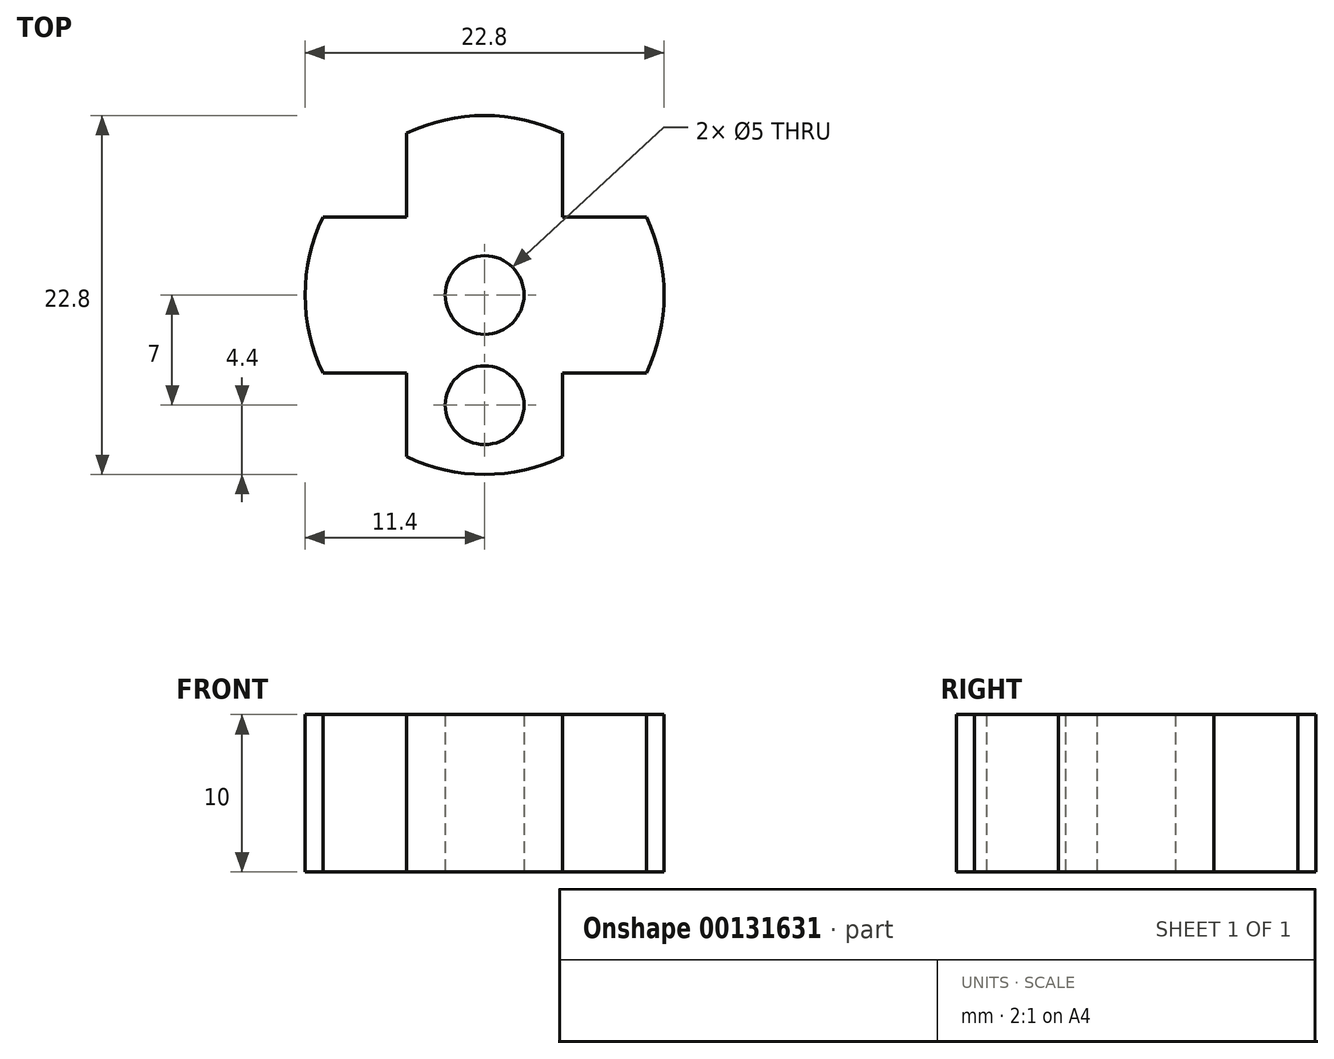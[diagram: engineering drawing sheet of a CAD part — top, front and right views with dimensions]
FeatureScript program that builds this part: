
annotation { "Feature Type Name" : "Feature", "Feature Type Description" : "" }
export const myFeature = defineFeature(function(context is Context, id is Id, definition is map)
    precondition{}
    {
        {
            var Q0;
            Q0=qCreatedBy(makeId("Top.planeOp"),FACE);
            var sketch = newSketch(context, id + "F0", { "sketchPlane" : qUnion([Q0])});
            skCircle(sketch, "E0", {"center": v(0, 0) * mm, "radius": 11.4 * mm});
            skCircle(sketch, "E1", {"center": v(0, 0) * mm, "radius": 2.5 * mm});
            skCircle(sketch, "E2", {"center": v(0, 0) * mm, "radius": 7 * mm, "construction": true});
            skCircle(sketch, "E3", {"center": v(0, -7) * mm, "radius": 2.5 * mm});
            skLineSegment(sketch, "E4", {"start": v(-4.95, -10.27) * mm, "end": v(-4.95, -4.95) * mm});
            skLineSegment(sketch, "E5", {"start": v(-4.95, -4.95) * mm, "end": v(-10.27, -4.95) * mm});
            skLineSegment(sketch, "E6.MirrorCS", {"start": v(4.95, -4.95) * mm, "end": v(10.27, -4.95) * mm});
            skLineSegment(sketch, "E7.MirrorCS", {"start": v(4.95, -10.27) * mm, "end": v(4.95, -4.95) * mm});
            skLineSegment(sketch, "E8.MirrorCS", {"start": v(-4.95, 4.95) * mm, "end": v(-10.27, 4.95) * mm});
            skLineSegment(sketch, "E9.MirrorCS", {"start": v(-4.95, 10.27) * mm, "end": v(-4.95, 4.95) * mm});
            skLineSegment(sketch, "E10.MirrorCS", {"start": v(4.95, 10.27) * mm, "end": v(4.95, 4.95) * mm});
            skLineSegment(sketch, "E11.MirrorCS", {"start": v(4.95, 4.95) * mm, "end": v(10.27, 4.95) * mm});
            skSolve(sketch);
        }
        {
            var Q0;
            Q0=makeQuery(id+"F0.imprint","IMPRINT",FACE,{"disambiguationData":[TD([[makeQuery(id+"F0.imprint","IMPRINT",EDGE,{"derivedFrom":sQuery(id+"F0.wireOp",EDGE,"E1")}),-1.0]])]});
            extrude(context, id + "F1", {"entities" : qUnion([Q0]), "depth" : 10 * mm});
        }
    });
